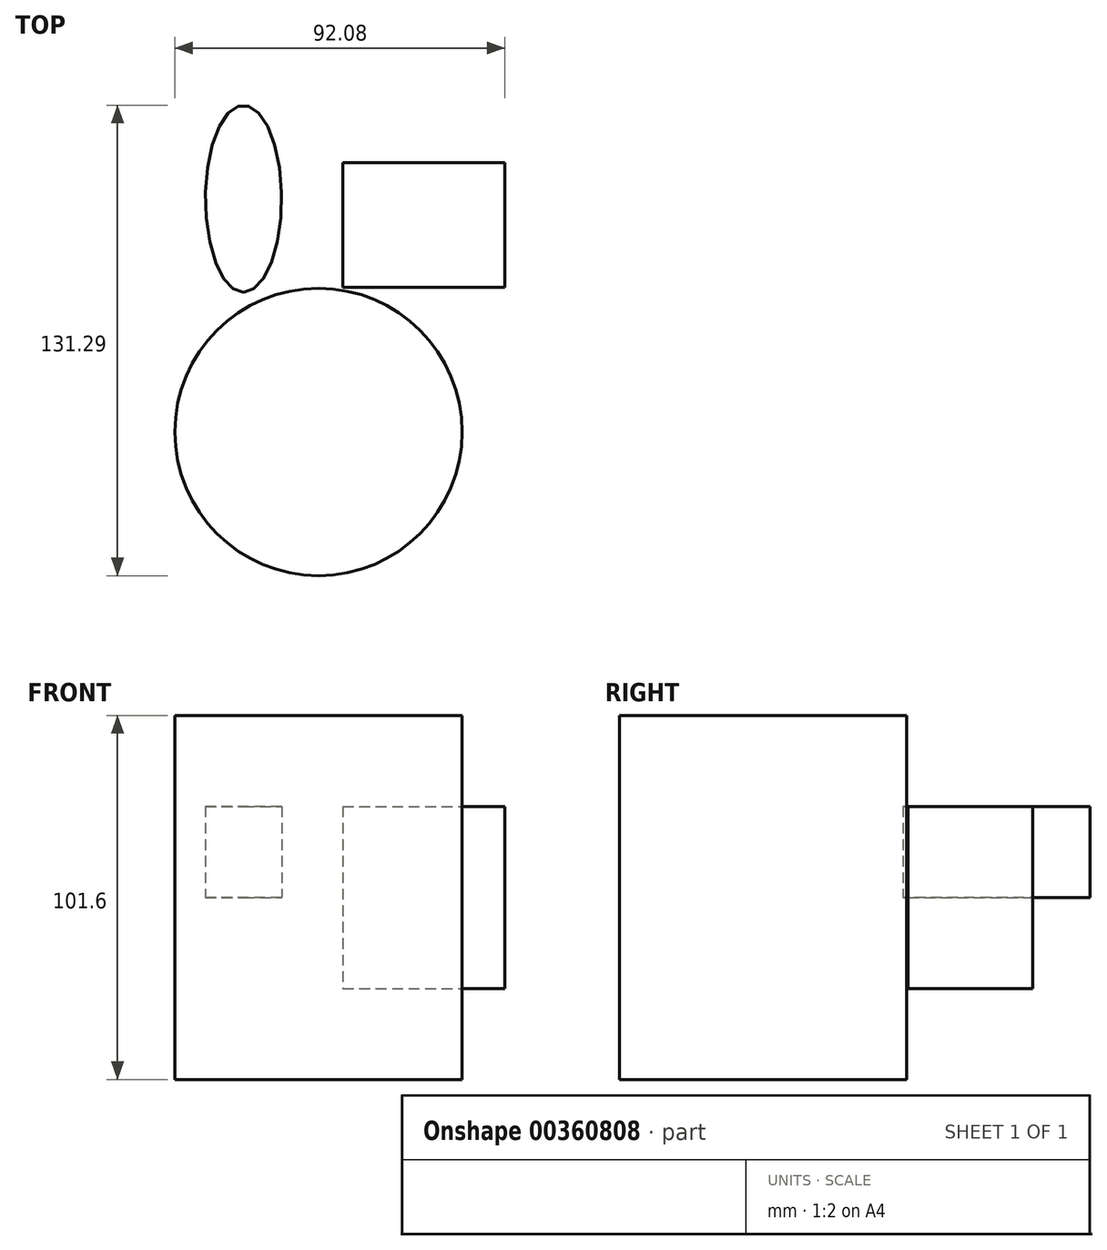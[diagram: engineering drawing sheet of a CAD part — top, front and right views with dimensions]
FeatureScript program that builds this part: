
annotation { "Feature Type Name" : "Feature", "Feature Type Description" : "" }
export const myFeature = defineFeature(function(context is Context, id is Id, definition is map)
    precondition{}
    {
        {
            var Q0;
            Q0=qCreatedBy(makeId("Top.planeOp"),FACE);
            var sketch = newSketch(context, id + "F0", { "sketchPlane" : qUnion([Q0])});
            skLineSegment(sketch, "E0.bottom", {"start": v(-14.88, 24.02) * mm, "end": v(30.35, 24.02) * mm});
            skLineSegment(sketch, "E0.top", {"start": v(-14.88, -10.76) * mm, "end": v(30.35, -10.76) * mm});
            skLineSegment(sketch, "E0.left", {"start": v(-14.88, 24.02) * mm, "end": v(-14.88, -10.76) * mm});
            skLineSegment(sketch, "E0.right", {"start": v(30.35, 24.02) * mm, "end": v(30.35, -10.76) * mm});
            skSolve(sketch);
        }
        {
            var Q0;
            Q0=makeQuery(id+"F0.imprint","IMPRINT",FACE,{"disambiguationData":[TD([[makeQuery(id+"F0.imprint","IMPRINT",EDGE,{"derivedFrom":sQuery(id+"F0.wireOp",EDGE,"E0.bottom")}),-1.0]])]});
            var Q1;
            Q1 = qSketchRegion(id + "F0", true);
            extrude(context, id + "F1", {"entities" : qUnion([Q0, Q1]), "depth" : 50.8 * mm});
        }
        {
            var Q0;
            Q0=qCreatedBy(makeId("Top.planeOp"),FACE);
            var sketch = newSketch(context, id + "F2", { "sketchPlane" : qUnion([Q0])});
            skLineSegment(sketch, "E1.0.0", {"start": v(-14.88, 24.02) * mm, "end": v(-14.88, -10.76) * mm});
            skLineSegment(sketch, "E1.0.1", {"start": v(-14.88, -10.76) * mm, "end": v(30.35, -10.76) * mm});
            skLineSegment(sketch, "E1.0.2", {"start": v(30.35, -10.76) * mm, "end": v(30.35, 24.02) * mm});
            skLineSegment(sketch, "E1.0.3", {"start": v(30.35, 24.02) * mm, "end": v(-14.88, 24.02) * mm});
            skLineSegment(sketch, "E2.0.2", {"start": v(30.35, -10.76) * mm, "end": v(-14.88, -10.76) * mm});
            skEllipse(sketch, "E3", {"center": v(-42.58, 13.93) * mm, "majorRadius": 26.1 * mm, "minorRadius": 10.63 * mm, "majorAxis": v(0, -1)});
            skSolve(sketch);
        }
        {
            var Q0;
            Q0 = qSketchRegion(id + "F2", true);
            extrude(context, id + "F3", {"entities" : qUnion([Q0]), "operationType" : NewBodyOperationType.ADD, "depth" : 50.8 * mm, "hasSecondDirection" : true, "secondDirectionOppositeDirection" : false, "secondDirectionDepth" : 25.4 * mm});
        }
        {
            var Q0;
            Q0=qCreatedBy(makeId("Top.planeOp"),FACE);
            var sketch = newSketch(context, id + "F4", { "sketchPlane" : qUnion([Q0])});
            skCircle(sketch, "E4", {"center": v(-21.65, -51.16) * mm, "radius": 18.82 * mm});
            skSolve(sketch);
        }
        {
            var Q0;
            Q0=qCreatedBy(makeId("Top.planeOp"),FACE);
            var sketch = newSketch(context, id + "F5", { "sketchPlane" : qUnion([Q0])});
            skCircle(sketch, "E5.0", {"center": v(-21.65, -51.16) * mm, "radius": 0.23 * mm});
            skCircle(sketch, "E6.0", {"center": v(-21.65, -51.16) * mm, "radius": 40.08 * mm});
            skSolve(sketch);
        }
        {
            var Q0;
            Q0 = qSketchRegion(id + "F4", true);
            extrude(context, id + "F6", {"entities" : qUnion([Q0]), "depth" : 50.8 * mm, "hasSecondDirection" : true, "secondDirectionOppositeDirection" : true, "secondDirectionDepth" : 25.4 * mm});
        }
        {
            var Q0;
            Q0 = qSketchRegion(id + "F4", true);
            var Q1;
            Q1 = qSketchRegion(id + "F5", true);
            extrude(context, id + "F7", {"entities" : qUnion([Q0, Q1]), "operationType" : NewBodyOperationType.ADD, "depth" : 76.2 * mm, "hasSecondDirection" : true, "secondDirectionOppositeDirection" : true, "secondDirectionDepth" : 25.4 * mm});
        }
        {
            var Q0;
            Q0=makeQuery(id+"F3.opExtrude","CAP_FACE",FACE,{"disambiguationData":[OSD([sQuery(id+"F2.wireOp",EDGE,"E3")])],"isStart":false});
            var Q1;
            Q1=sQuery(id+"F2.wireOp",EDGE,"E3");
            extrude(context, id + "F8", {"entities" : qUnion([Q0]), "bodyType" : ToolBodyType.SURFACE, "surfaceEntities" : qUnion([Q1]), "depth" : 25.4 * mm});
        }
    });
